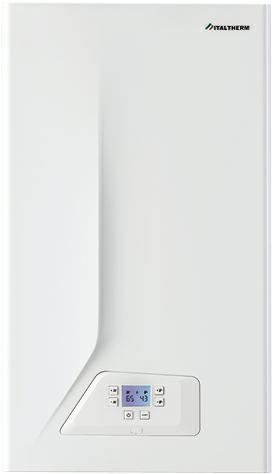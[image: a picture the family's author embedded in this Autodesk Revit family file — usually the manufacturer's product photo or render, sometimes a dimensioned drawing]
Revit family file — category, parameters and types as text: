
# Revit family: City Class H KR
name_source: partatom
category: Attrezzatura meccanica
units: mm (PartAtom-declared; Revit-internal decimal feet)

## family parameters
Classificazione = Nessuno
Condiviso = No
Host = Muro
Mantieni orientamento annotazione = No
Punto di calcolo locali = No
Quota connettore circolare = Usa diametro
Sempre verticale = Sì
Taglio con vuoti quando caricato = No
Tipo di parte = Normale

## types (2) — shared parameters
Combustion air inlet - separate system = 80 mm  [stored 0.262467 ft]
Date of publishing = 22/07/2019
Depth = 324 mm  [stored 1.06299 ft]
Design country = Italy
Domestic Cold Water Diameter = 21 mm  [stored 0.0688976 ft]
Domestic Hot Water Diameter = 21 mm  [stored 0.0688976 ft]
Energetic efficiency (92/42/CEE) = n.d.
Flue outlet = 100 mm  [stored 0.328084 ft]
Gas Inlet Diameter = 26 mm
Height = 700 mm  [stored 2.29659 ft]
Hydronic Return Diameter = 26 mm
Hydronic Supply Diameter = 26 mm
IFC Classification = Boiler
Immagine tipo = city class.jpg
Manufacturer country = Italy
Manufacturer name = Italtherm S.p.A.
Material main = Metal
Material secondary = Plastic
NBS reference Description = Boilers
Omniclass Description = Condensing boilers
Power supply | Frequency (Hz) = 50
Power supply | Phase = 1
Power supply | Voltage (V) = 230 V
Product family = Heating
Product group = Thermal unit
Siphon with condensate drain = 25 mm  [stored 0.082021 ft]
Uniclass 2015 Name = Boilers
Width = 400 mm  [stored 1.31234 ft]
zero-valued in all types: Edition number, Prospetto di default

## per-type parameters (varying)
| type | Efficiency 30% | Maximum heat output 50/30°C | Maximum heat output 80/60°C | Maximum heating heat input | Minimum heat output 50/30°C | Minimum heat output 80/60°C | Nominal efficiency 50/30°C | Nominal efficiency 80/60°C | Power consumption (W) | URL | URL ENG | Weight |
| City Class H 25 KR | 106.2 | 22.1 | 20.3 | 21 | 2.7 | 2.4 | 105.8 | 95.9 | 75 | www.italtherm.it/g/caldaia-a-gas-da-interno/caldaia-a-condensazione/city-class-k/25-kw | en.italtherm.it/g/wall-hung-condensing-boilers/gas-boiler/city-class-k/25-kw | 28.50 kg |
| City Class H 35 KR | 106.9 | 29 | 26.3 | 28 | 3.7 | 3.2 | 105.1 | 95.2 | 107 | www.italtherm.it/g/caldaia-a-gas-da-interno/caldaia-a-condensazione/city-class-k/35-kw | en.italtherm.it/g/wall-hung-condensing-boilers/gas-boiler/city-class-k/35-kw | 34.00 kg |

note: [stored X ft] marks values corroborated as IEEE doubles in the binary element streams (Revit-internal decimal feet)
